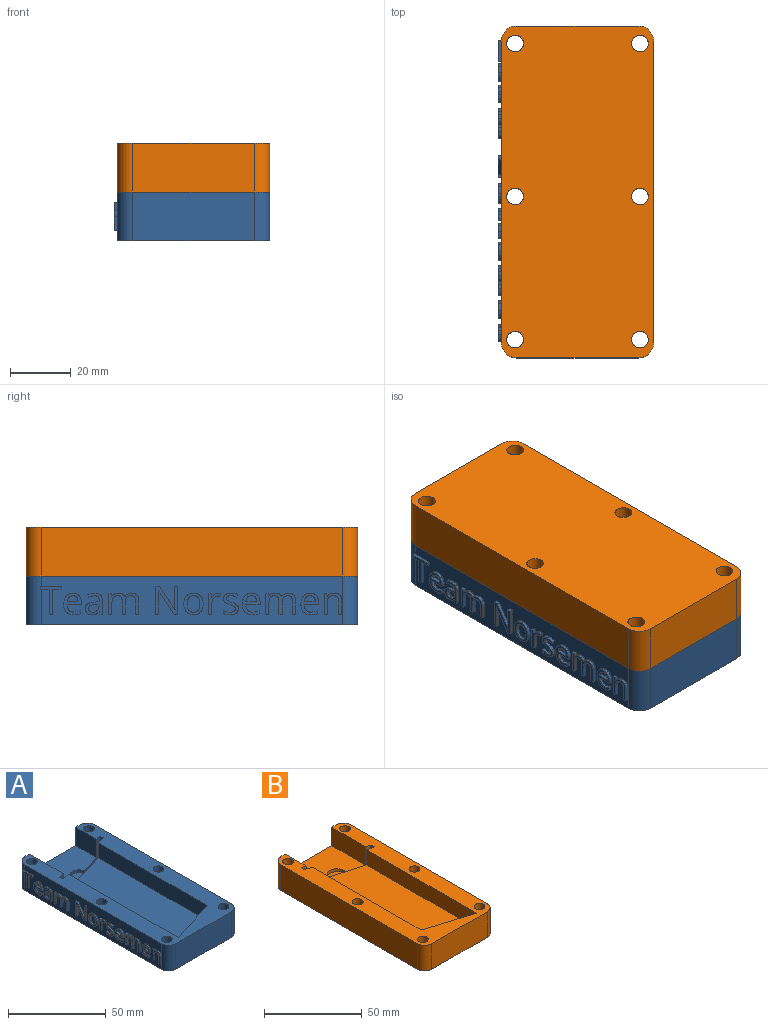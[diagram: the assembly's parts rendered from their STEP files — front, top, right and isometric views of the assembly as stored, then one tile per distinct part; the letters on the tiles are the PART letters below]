
ASSEMBLY  parts=2 mates=1
PART A: 282 faces, bbox 51x109x16 mm
  f0: plane 99x16mm, normal (-1,0,0), area 1307.5mm2, adj f2,f3,f26,f27,f28,f29,f30,f32
  f1: plane 40x16mm, normal (0,1,0), area 254.7mm2, adj f2,f3,f17,f18,f19,f278,f279
  f2: plane 109x50mm, normal (0,0,1), area 2115.1mm2, adj f0,f1,f4,f5,f6,f7,f8,f10
  f3: plane 109x50mm, normal (0,0,-1), area 5286mm2, adj f0,f1,f4,f5,f10,f11,f12,f13
  f4: plane 99x16mm, normal (1,0,0), area 1584mm2, adj f2,f3,f279,f281
  f5: plane 40x16mm, normal (0,-1,0), area 640mm2, adj f2,f3,f280,f281
  f6: plane 79.43x9.5mm, normal (1,0,0), area 754.5mm2, adj f2,f7,f9,f16
  f7: plane 30.5x9.5mm, normal (-0.3,0.95,0), area 303.5mm2, adj f2,f6,f8,f9
  f8: plane 78.57x9.5mm, normal (-1,0,0), area 746.5mm2, adj f2,f7,f9,f16
  f9: plane 88.07x30.5mm, normal (0,0,1), area 2409.5mm2, adj f6,f7,f8,f16
  f10: cylinder r=2.75mm len=16mm, axis (0,0,1), area 276.5mm2, adj f2,f3
  f11: cylinder r=2.75mm len=16mm, axis (0,0,1), area 276.5mm2, adj f2,f3
  f12: cylinder r=2.75mm len=16mm, axis (0,0,1), area 276.5mm2, adj f2,f3
  f13: cylinder r=2.75mm len=16mm, axis (0,0,1), area 276.5mm2, adj f2,f3
  f14: cylinder r=2.75mm len=16mm, axis (0,0,1), area 276.5mm2, adj f2,f3
  f15: cylinder r=2.75mm len=16mm, axis (0,0,1), area 276.5mm2, adj f2,f3
  f16: plane 39.93x13.3mm, normal (-0.27,0.96,0), area 250.8mm2, adj f2,f6,f8,f9,f21,f24,f25
  f17: plane 24.51x11.5mm, normal (1,0,0), area 281.8mm2, adj f1,f2,f19,f20
  f18: plane 15.01x11.5mm, normal (-1,0,0), area 172.6mm2, adj f1,f2,f19,f22
  f19: plane 33.5x24.51mm, normal (0,0,1), area 622.5mm2, adj f1,f17,f18,f20,f22,f23
  f20: plane 15.15x13.3mm, normal (0.27,-0.96,0), area 74.6mm2, adj f2,f17,f19,f23,f24,f25
  f21: plane 13.3x2.31mm, normal (-0.96,-0.27,0), area 31.9mm2, adj f2,f16,f22,f25
  f22: plane 15.15x13.3mm, normal (0.27,-0.96,0), area 58.9mm2, adj f2,f18,f19,f21,f23,f25
  f23: cylinder r=5mm len=9.81mm, axis (0,0,1), area 28.3mm2, adj f19,f20,f22,f25
  f24: plane 13.3x2.31mm, normal (0.96,0.27,0), area 31.9mm2, adj f2,f16,f20,f25
  f25: plane 40.58x13.63mm, normal (0,0,1), area 138.9mm2, adj f16,f20,f21,f22,f23,f24
  f26: plane 1.07x1mm, normal (0,0,-1), area 1.1mm2, adj f0,f27,f33,f34
  f27: plane 8.26x1mm, normal (0,-1,0), area 8.3mm2, adj f0,f26,f28,f34
  f28: plane 2.92x1mm, normal (0,0,-1), area 2.9mm2, adj f0,f27,f29,f34
  f29: plane 1x0.95mm, normal (0,-1,0), area 1mm2, adj f0,f28,f30,f34
  f30: plane 6.9x1.02mm, normal (0,0,1), area 6.9mm2, adj f0,f29,f31,f34,f278
  f31: plane 1.02x0.95mm, normal (0,1,0), area 1mm2, adj f30,f32,f34,f278
  f32: plane 2.92x1.02mm, normal (0,0,-1), area 2.9mm2, adj f0,f31,f33,f34,f278
  f33: plane 8.26x1mm, normal (0,1,0), area 8.3mm2, adj f0,f26,f32,f34
  f34: plane 9.21x6.9mm, normal (-1,0,0), area 15.4mm2, adj f26,f27,f28,f29,f30,f31,f32,f33
  f35: extruded ~1.33x1mm, area 1.5mm2, adj f36,f53,f54,f55
  f36: extruded ~1.26x1mm, area 1.4mm2, adj f35,f37,f54,f55
  f37: extruded ~1.51x1mm, area 1.6mm2, adj f36,f38,f54,f55
  f38: plane 3.61x1mm, normal (0,0,1), area 3.6mm2, adj f37,f53,f54,f55
  f39: extruded ~2.42x1mm, area 2.7mm2, adj f0,f40,f52,f54
  f40: extruded ~1.19x1mm, area 1.2mm2, adj f0,f39,f41,f54
  f41: extruded ~1.05x1mm, area 1.1mm2, adj f0,f40,f42,f54
  f42: plane 1x0.93mm, normal (0,-1,0), area 0.9mm2, adj f0,f41,f43,f54
  f43: extruded ~2.2x1mm, area 2.3mm2, adj f0,f42,f44,f54
  f44: extruded ~1.64x1mm, area 1.8mm2, adj f0,f43,f45,f54
  f45: extruded ~1.84x1mm, area 2mm2, adj f0,f44,f46,f54
  f46: plane 4.75x1mm, normal (0,0,-1), area 4.8mm2, adj f0,f45,f47,f54
  f47: plane 1x0.66mm, normal (0,-1,0), area 0.7mm2, adj f0,f46,f48,f54
  f48: extruded ~2.25x1mm, area 2.4mm2, adj f0,f47,f49,f54
  f49: extruded ~2.05x1mm, area 2.3mm2, adj f0,f48,f50,f54
  f50: extruded ~2.21x1mm, area 2.5mm2, adj f0,f49,f51,f54
  f51: extruded ~2.65x1mm, area 2.8mm2, adj f0,f50,f52,f54
  f52: extruded ~2.59x1mm, area 2.8mm2, adj f0,f39,f51,f54
  f53: extruded ~1.5x1mm, area 1.6mm2, adj f35,f38,f54,f55
  f54: plane 7.16x5.84mm, normal (-1,0,0), area 19mm2, adj f35,f36,f37,f38,f39,f40,f41,f42
  f55: plane 3.61x2.04mm, normal (-1,0,0), area 5.9mm2, adj f35,f36,f37,f38,f53
  f56: extruded ~1.53x1mm, area 1.7mm2, adj f57,f82,f83,f84
  f57: extruded ~1x0.96mm, area 1mm2, adj f56,f58,f83,f84
  f58: extruded ~1x0.86mm, area 1mm2, adj f57,f59,f83,f84
  f59: extruded ~1.07x1mm, area 1.3mm2, adj f58,f60,f83,f84
  f60: extruded ~1.8x1mm, area 1.9mm2, adj f59,f61,f83,f84
  f61: plane 1.05x1mm, normal (0,-0.04,-1), area 1mm2, adj f60,f62,f83,f84
  f62: plane 1x0.62mm, normal (0,1,0), area 0.6mm2, adj f61,f82,f83,f84
  f63: plane 1x0.98mm, normal (0,0.98,-0.21), area 1mm2, adj f0,f64,f81,f83
  f64: plane 1x0.78mm, normal (0,0,-1), area 0.8mm2, adj f0,f63,f65,f83
  f65: plane 4.71x1mm, normal (0,-1,0), area 4.7mm2, adj f0,f64,f66,f83
  f66: extruded ~1.76x1mm, area 1.9mm2, adj f0,f65,f67,f83
  f67: extruded ~1.83x1mm, area 2mm2, adj f0,f66,f68,f83
  f68: extruded ~1.22x1mm, area 1.2mm2, adj f0,f67,f69,f83
  f69: extruded ~1.12x1mm, area 1.2mm2, adj f0,f68,f70,f83
  f70: plane 1x0.8mm, normal (0,0.93,-0.37), area 0.9mm2, adj f0,f69,f71,f83
  f71: extruded ~1.95x1mm, area 2mm2, adj f0,f70,f72,f83
  f72: extruded ~1.12x1mm, area 1.2mm2, adj f0,f71,f73,f83
  f73: extruded ~1.2x1mm, area 1.3mm2, adj f0,f72,f74,f83
  f74: plane 1x0.43mm, normal (0,1,0), area 0.4mm2, adj f0,f73,f75,f83
  f75: plane 1.17x1mm, normal (0,0.03,1), area 1.2mm2, adj f0,f74,f76,f83
  f76: extruded ~3.34x2.19mm, area 4.5mm2, adj f0,f75,f77,f83
  f77: extruded ~1.51x1mm, area 1.7mm2, adj f0,f76,f78,f83
  f78: extruded ~1.61x1mm, area 1.7mm2, adj f0,f77,f79,f83
  f79: extruded ~1.28x1mm, area 1.3mm2, adj f0,f78,f80,f83
  f80: extruded ~1.03x1mm, area 1.4mm2, adj f0,f79,f81,f83
  f81: plane 1x0.05mm, normal (0,0,-1), area 0.1mm2, adj f0,f63,f80,f83
  f82: extruded ~1.5x1mm, area 1.6mm2, adj f56,f62,f83,f84
  f83: plane 7.14x5.54mm, normal (-1,0,0), area 18.7mm2, adj f56,f57,f58,f59,f60,f61,f62,f63
  f84: plane 3.39x2.66mm, normal (-1,0,0), area 7.3mm2, adj f56,f57,f58,f59,f60,f61,f62,f82
  f85: plane 4.49x1mm, normal (0,1,0), area 4.5mm2, adj f0,f86,f112,f113
  f86: plane 1.04x1mm, normal (0,0,-1), area 1mm2, adj f0,f85,f87,f113
  f87: plane 4.5x1mm, normal (0,-1,0), area 4.5mm2, adj f0,f86,f88,f113
  f88: extruded ~1.93x1mm, area 2.1mm2, adj f0,f87,f89,f113
  f89: extruded ~1.75x1mm, area 1.9mm2, adj f0,f88,f90,f113
  f90: extruded ~1.34x1mm, area 1.4mm2, adj f0,f89,f91,f113
  f91: extruded ~1x0.89mm, area 1.3mm2, adj f0,f90,f92,f113
  f92: plane 1x0.05mm, normal (0,0,1), area 0.1mm2, adj f0,f91,f93,f113
  f93: extruded ~2.12x1.17mm, area 2.6mm2, adj f0,f92,f94,f113
  f94: extruded ~1.21x1mm, area 1.3mm2, adj f0,f93,f95,f113
  f95: extruded ~1x0.84mm, area 1.2mm2, adj f0,f94,f96,f113
  f96: plane 1x0.05mm, normal (0,0,1), area 0.1mm2, adj f0,f95,f97,f113
  f97: plane 1x0.95mm, normal (0,-0.98,0.18), area 1mm2, adj f0,f96,f98,f113
  f98: plane 1x0.85mm, normal (0,0,1), area 0.9mm2, adj f0,f97,f99,f113
  f99: plane 6.9x1mm, normal (0,1,0), area 6.9mm2, adj f0,f98,f100,f113
  f100: plane 1.05x1mm, normal (0,0,-1), area 1mm2, adj f0,f99,f101,f113
  f101: plane 3.62x1mm, normal (0,-1,0), area 3.6mm2, adj f0,f100,f102,f113
  f102: extruded ~1.93x1mm, area 2mm2, adj f0,f101,f103,f113
  f103: extruded ~1.44x1mm, area 1.6mm2, adj f0,f102,f104,f113
  f104: extruded ~1.1x1mm, area 1.2mm2, adj f0,f103,f105,f113
  f105: extruded ~1.24x1mm, area 1.3mm2, adj f0,f104,f106,f113
  f106: plane 4.49x1mm, normal (0,1,0), area 4.5mm2, adj f0,f105,f107,f113
  f107: plane 1.05x1mm, normal (0,0,-1), area 1mm2, adj f0,f106,f108,f113
  f108: plane 3.85x1mm, normal (0,-1,0), area 3.9mm2, adj f0,f107,f109,f113
  f109: extruded ~1.73x1mm, area 1.8mm2, adj f0,f108,f110,f113
  f110: extruded ~1.44x1mm, area 1.6mm2, adj f0,f109,f111,f113
  f111: extruded ~1.1x1mm, area 1.2mm2, adj f0,f110,f112,f113
  f112: extruded ~1.24x1mm, area 1.3mm2, adj f0,f85,f111,f113
  f113: plane 9.84x7.03mm, normal (-1,0,0), area 27mm2, adj f85,f86,f87,f88,f89,f90,f91,f92
  f114: plane 1.22x1mm, normal (0,0,-1), area 1.2mm2, adj f0,f115,f128,f129
  f115: plane 9.21x1mm, normal (0,-1,0), area 9.2mm2, adj f0,f114,f116,f129
  f116: plane 1x1mm, normal (0,0,1), area 1mm2, adj f0,f115,f117,f129
  f117: plane 5.28x1mm, normal (0,1,0), area 5.3mm2, adj f0,f116,f118,f129
  f118: extruded ~1.32x1mm, area 1.3mm2, adj f0,f117,f119,f129
  f119: extruded ~1.09x1mm, area 1.1mm2, adj f0,f118,f120,f129
  f120: plane 1x0.05mm, normal (0,0,1), area 0.1mm2, adj f0,f119,f121,f129
  f121: plane 7.7x5.02mm, normal (0,-0.84,0.55), area 9.2mm2, adj f0,f120,f122,f129
  f122: plane 1.21x1mm, normal (0,0,1), area 1.2mm2, adj f0,f121,f123,f129
  f123: plane 9.21x1mm, normal (0,1,0), area 9.2mm2, adj f0,f122,f124,f129
  f124: plane 1x0.99mm, normal (0,0,-1), area 1mm2, adj f0,f123,f125,f129
  f125: plane 5.23x1mm, normal (0,-1,0), area 5.2mm2, adj f0,f124,f126,f129
  f126: extruded ~2.49x1mm, area 2.5mm2, adj f0,f125,f127,f129
  f127: plane 1x0.05mm, normal (0,0,-1), area 0.1mm2, adj f0,f126,f128,f129
  f128: plane 7.73x5.03mm, normal (0,0.84,-0.55), area 9.2mm2, adj f0,f114,f127,f129
  f129: plane 9.21x7.19mm, normal (-1,0,0), area 28mm2, adj f114,f115,f116,f117,f118,f119,f120,f121
  f130: extruded ~2.02x1mm, area 2.1mm2, adj f131,f146,f147,f148
  f131: extruded ~2.01x1mm, area 2.1mm2, adj f130,f132,f147,f148
  f132: extruded ~1.55x1mm, area 1.8mm2, adj f131,f133,f147,f148
  f133: extruded ~1.57x1mm, area 1.8mm2, adj f132,f134,f147,f148
  f134: extruded ~2x1mm, area 2.1mm2, adj f133,f135,f147,f148
  f135: extruded ~2.02x1mm, area 2.1mm2, adj f134,f136,f147,f148
  f136: extruded ~1.56x1mm, area 1.8mm2, adj f135,f146,f147,f148
  f137: extruded ~2.64x1mm, area 2.8mm2, adj f0,f138,f145,f147
  f138: extruded ~2.61x1mm, area 2.8mm2, adj f0,f137,f139,f147
  f139: extruded ~2.3x1mm, area 2.6mm2, adj f0,f138,f140,f147
  f140: extruded ~2.34x1mm, area 2.6mm2, adj f0,f139,f141,f147
  f141: extruded ~2.63x1mm, area 2.8mm2, adj f0,f140,f142,f147
  f142: extruded ~1.9x1mm, area 2mm2, adj f0,f141,f143,f147
  f143: extruded ~1.25x1.11mm, area 1.7mm2, adj f0,f142,f144,f147
  f144: extruded ~1.64x1mm, area 1.7mm2, adj f0,f143,f145,f147
  f145: extruded ~2.35x1mm, area 2.6mm2, adj f0,f137,f144,f147
  f146: extruded ~1.55x1mm, area 1.8mm2, adj f130,f136,f147,f148
  f147: plane 7.16x6.34mm, normal (-1,0,0), area 18.3mm2, adj f130,f131,f132,f133,f134,f135,f136,f137
  f148: plane 5.39x4.18mm, normal (-1,0,0), area 18.7mm2, adj f130,f131,f132,f133,f134,f135,f136,f146
  f149: extruded ~1x0.82mm, area 0.8mm2, adj f0,f150,f161,f162
  f150: extruded ~1.19x1mm, area 1.3mm2, adj f0,f149,f151,f162
  f151: extruded ~1.04x1mm, area 1.4mm2, adj f0,f150,f152,f162
  f152: plane 1x0.05mm, normal (0,0,1), area 0.1mm2, adj f0,f151,f153,f162
  f153: plane 1.28x1mm, normal (0,-1,0.09), area 1.3mm2, adj f0,f152,f154,f162
  f154: plane 1x0.86mm, normal (0,0,1), area 0.9mm2, adj f0,f153,f155,f162
  f155: plane 6.9x1mm, normal (0,1,0), area 6.9mm2, adj f0,f154,f156,f162
  f156: plane 1.05x1mm, normal (0,0,-1), area 1mm2, adj f0,f155,f157,f162
  f157: plane 3.7x1mm, normal (0,-1,0), area 3.7mm2, adj f0,f156,f158,f162
  f158: extruded ~1.69x1mm, area 1.8mm2, adj f0,f157,f159,f162
  f159: extruded ~1.43x1mm, area 1.6mm2, adj f0,f158,f160,f162
  f160: extruded ~1x0.76mm, area 0.8mm2, adj f0,f159,f161,f162
  f161: plane 1x0.97mm, normal (0,-0.99,-0.15), area 1mm2, adj f0,f149,f160,f162
  f162: plane 7.03x3.97mm, normal (-1,0,0), area 9.9mm2, adj f149,f150,f151,f152,f153,f154,f155,f156
  f163: extruded ~1.49x1mm, area 1.7mm2, adj f0,f164,f187,f188
  f164: extruded ~1.14x1mm, area 1.3mm2, adj f0,f163,f165,f188
  f165: extruded ~1.66x1mm, area 1.9mm2, adj f0,f164,f166,f188
  f166: extruded ~1.21x1mm, area 1.3mm2, adj f0,f165,f167,f188
  f167: extruded ~1x0.46mm, area 0.6mm2, adj f0,f166,f168,f188
  f168: extruded ~1x0.47mm, area 0.5mm2, adj f0,f167,f169,f188
  f169: extruded ~1x0.64mm, area 0.8mm2, adj f0,f168,f170,f188
  f170: extruded ~1.12x1mm, area 1.2mm2, adj f0,f169,f171,f188
  f171: extruded ~1.88x1mm, area 1.9mm2, adj f0,f170,f172,f188
  f172: plane 1x0.85mm, normal (0,-0.92,-0.4), area 0.9mm2, adj f0,f171,f173,f188
  f173: extruded ~2.18x1mm, area 2.2mm2, adj f0,f172,f174,f188
  f174: extruded ~1.88x1mm, area 2mm2, adj f0,f173,f175,f188
  f175: extruded ~1.33x1mm, area 1.6mm2, adj f0,f174,f176,f188
  f176: extruded ~1x0.81mm, area 0.8mm2, adj f0,f175,f177,f188
  f177: extruded ~1x0.61mm, area 0.9mm2, adj f0,f176,f178,f188
  f178: extruded ~1.37x1mm, area 1.5mm2, adj f0,f177,f179,f188
  f179: extruded ~1.36x1mm, area 1.5mm2, adj f0,f178,f180,f188
  f180: extruded ~1x0.69mm, area 0.8mm2, adj f0,f179,f181,f188
  f181: extruded ~1x0.8mm, area 1mm2, adj f0,f180,f182,f188
  f182: extruded ~1.26x1mm, area 1.3mm2, adj f0,f181,f183,f188
  f183: extruded ~1.1x1mm, area 1.1mm2, adj f0,f182,f184,f188
  f184: extruded ~1.07x1mm, area 1.1mm2, adj f0,f183,f185,f188
  f185: plane 1x0.97mm, normal (0,1,0), area 1mm2, adj f0,f184,f186,f188
  f186: extruded ~2.14x1mm, area 2.2mm2, adj f0,f185,f187,f188
  f187: extruded ~2.02x1mm, area 2.1mm2, adj f0,f163,f186,f188
  f188: plane 7.16x4.89mm, normal (-1,0,0), area 14.6mm2, adj f163,f164,f165,f166,f167,f168,f169,f170
  f189: extruded ~1.33x1mm, area 1.5mm2, adj f190,f207,f208,f209
  f190: extruded ~1.26x1mm, area 1.4mm2, adj f189,f191,f208,f209
  f191: extruded ~1.51x1mm, area 1.6mm2, adj f190,f192,f208,f209
  f192: plane 3.61x1mm, normal (0,0,1), area 3.6mm2, adj f191,f207,f208,f209
  f193: extruded ~2.42x1mm, area 2.7mm2, adj f0,f194,f206,f208
  f194: extruded ~1.19x1mm, area 1.2mm2, adj f0,f193,f195,f208
  f195: extruded ~1.05x1mm, area 1.1mm2, adj f0,f194,f196,f208
  f196: plane 1x0.93mm, normal (0,-1,0), area 0.9mm2, adj f0,f195,f197,f208
  f197: extruded ~2.2x1mm, area 2.3mm2, adj f0,f196,f198,f208
  f198: extruded ~1.64x1mm, area 1.8mm2, adj f0,f197,f199,f208
  f199: extruded ~1.84x1mm, area 2mm2, adj f0,f198,f200,f208
  f200: plane 4.75x1mm, normal (0,0,-1), area 4.8mm2, adj f0,f199,f201,f208
  f201: plane 1x0.66mm, normal (0,-1,0), area 0.7mm2, adj f0,f200,f202,f208
  f202: extruded ~2.25x1mm, area 2.4mm2, adj f0,f201,f203,f208
  f203: extruded ~2.05x1mm, area 2.3mm2, adj f0,f202,f204,f208
  f204: extruded ~2.21x1mm, area 2.5mm2, adj f0,f203,f205,f208
  f205: extruded ~2.65x1mm, area 2.8mm2, adj f0,f204,f206,f208
  f206: extruded ~2.59x1mm, area 2.8mm2, adj f0,f193,f205,f208
  f207: extruded ~1.5x1mm, area 1.6mm2, adj f189,f192,f208,f209
  f208: plane 7.16x5.84mm, normal (-1,0,0), area 19mm2, adj f189,f190,f191,f192,f193,f194,f195,f196
  f209: plane 3.61x2.04mm, normal (-1,0,0), area 5.9mm2, adj f189,f190,f191,f192,f207
  f210: plane 4.49x1mm, normal (0,1,0), area 4.5mm2, adj f0,f211,f237,f238
  f211: plane 1.04x1mm, normal (0,0,-1), area 1mm2, adj f0,f210,f212,f238
  f212: plane 4.5x1mm, normal (0,-1,0), area 4.5mm2, adj f0,f211,f213,f238
  f213: extruded ~1.93x1mm, area 2.1mm2, adj f0,f212,f214,f238
  f214: extruded ~1.75x1mm, area 1.9mm2, adj f0,f213,f215,f238
  f215: extruded ~1.34x1mm, area 1.4mm2, adj f0,f214,f216,f238
  f216: extruded ~1x0.89mm, area 1.3mm2, adj f0,f215,f217,f238
  f217: plane 1x0.05mm, normal (0,0,1), area 0.1mm2, adj f0,f216,f218,f238
  f218: extruded ~2.12x1.17mm, area 2.6mm2, adj f0,f217,f219,f238
  f219: extruded ~1.21x1mm, area 1.3mm2, adj f0,f218,f220,f238
  f220: extruded ~1x0.84mm, area 1.2mm2, adj f0,f219,f221,f238
  f221: plane 1x0.05mm, normal (0,0,1), area 0.1mm2, adj f0,f220,f222,f238
  f222: plane 1x0.95mm, normal (0,-0.98,0.18), area 1mm2, adj f0,f221,f223,f238
  f223: plane 1x0.85mm, normal (0,0,1), area 0.9mm2, adj f0,f222,f224,f238
  f224: plane 6.9x1mm, normal (0,1,0), area 6.9mm2, adj f0,f223,f225,f238
  f225: plane 1.05x1mm, normal (0,0,-1), area 1mm2, adj f0,f224,f226,f238
  f226: plane 3.62x1mm, normal (0,-1,0), area 3.6mm2, adj f0,f225,f227,f238
  f227: extruded ~1.93x1mm, area 2mm2, adj f0,f226,f228,f238
  f228: extruded ~1.44x1mm, area 1.6mm2, adj f0,f227,f229,f238
  f229: extruded ~1.1x1mm, area 1.2mm2, adj f0,f228,f230,f238
  f230: extruded ~1.24x1mm, area 1.3mm2, adj f0,f229,f231,f238
  f231: plane 4.49x1mm, normal (0,1,0), area 4.5mm2, adj f0,f230,f232,f238
  f232: plane 1.05x1mm, normal (0,0,-1), area 1mm2, adj f0,f231,f233,f238
  f233: plane 3.85x1mm, normal (0,-1,0), area 3.9mm2, adj f0,f232,f234,f238
  f234: extruded ~1.73x1mm, area 1.8mm2, adj f0,f233,f235,f238
  f235: extruded ~1.44x1mm, area 1.6mm2, adj f0,f234,f236,f238
  f236: extruded ~1.1x1mm, area 1.2mm2, adj f0,f235,f237,f238
  f237: extruded ~1.24x1mm, area 1.3mm2, adj f0,f210,f236,f238
  f238: plane 9.84x7.03mm, normal (-1,0,0), area 27mm2, adj f210,f211,f212,f213,f214,f215,f216,f217
  f239: extruded ~1.33x1mm, area 1.5mm2, adj f240,f257,f258,f259
  f240: extruded ~1.26x1mm, area 1.4mm2, adj f239,f241,f258,f259
  f241: extruded ~1.51x1mm, area 1.6mm2, adj f240,f242,f258,f259
  f242: plane 3.61x1mm, normal (0,0,1), area 3.6mm2, adj f241,f257,f258,f259
  f243: extruded ~2.42x1mm, area 2.7mm2, adj f0,f244,f256,f258
  f244: extruded ~1.19x1mm, area 1.2mm2, adj f0,f243,f245,f258
  f245: extruded ~1.05x1mm, area 1.1mm2, adj f0,f244,f246,f258
  f246: plane 1x0.93mm, normal (0,-1,0), area 0.9mm2, adj f0,f245,f247,f258
  f247: extruded ~2.2x1mm, area 2.3mm2, adj f0,f246,f248,f258
  f248: extruded ~1.64x1mm, area 1.8mm2, adj f0,f247,f249,f258
  f249: extruded ~1.84x1mm, area 2mm2, adj f0,f248,f250,f258
  f250: plane 4.75x1mm, normal (0,0,-1), area 4.8mm2, adj f0,f249,f251,f258
  f251: plane 1x0.66mm, normal (0,-1,0), area 0.7mm2, adj f0,f250,f252,f258
  f252: extruded ~2.25x1mm, area 2.4mm2, adj f0,f251,f253,f258
  f253: extruded ~2.05x1mm, area 2.3mm2, adj f0,f252,f254,f258
  f254: extruded ~2.21x1mm, area 2.5mm2, adj f0,f253,f255,f258
  f255: extruded ~2.65x1mm, area 2.8mm2, adj f0,f254,f256,f258
  f256: extruded ~2.59x1mm, area 2.8mm2, adj f0,f243,f255,f258
  f257: extruded ~1.5x1mm, area 1.6mm2, adj f239,f242,f258,f259
  f258: plane 7.16x5.84mm, normal (-1,0,0), area 19mm2, adj f239,f240,f241,f242,f243,f244,f245,f246
  f259: plane 3.61x2.04mm, normal (-1,0,0), area 5.9mm2, adj f239,f240,f241,f242,f257
  f260: plane 4.47x1mm, normal (0,1,0), area 4.5mm2, adj f0,f261,f276,f277
  f261: plane 1.05x1mm, normal (0,0,-1), area 1mm2, adj f0,f260,f262,f277
  f262: plane 4.5x1mm, normal (0,-1,0), area 4.5mm2, adj f0,f261,f263,f277
  f263: extruded ~1.93x1mm, area 2.1mm2, adj f0,f262,f264,f277
  f264: extruded ~1.88x1mm, area 2mm2, adj f0,f263,f265,f277
  f265: extruded ~1.29x1mm, area 1.3mm2, adj f0,f264,f266,f277
  f266: extruded ~1x0.9mm, area 1.2mm2, adj f0,f265,f267,f277
  f267: plane 1x0.05mm, normal (0,0,1), area 0.1mm2, adj f0,f266,f268,f277
  f268: plane 1x0.95mm, normal (0,-0.98,0.18), area 1mm2, adj f0,f267,f269,f277
  f269: plane 1x0.85mm, normal (0,0,1), area 0.9mm2, adj f0,f268,f270,f277
  f270: plane 6.9x1mm, normal (0,1,0), area 6.9mm2, adj f0,f269,f271,f277
  f271: plane 1.05x1mm, normal (0,0,-1), area 1mm2, adj f0,f270,f272,f277
  f272: plane 3.62x1mm, normal (0,-1,0), area 3.6mm2, adj f0,f271,f273,f277
  f273: extruded ~1.93x1mm, area 2mm2, adj f0,f272,f274,f277
  f274: extruded ~1.59x1mm, area 1.7mm2, adj f0,f273,f275,f277
  f275: extruded ~1.2x1mm, area 1.3mm2, adj f0,f274,f276,f277
  f276: extruded ~1.26x1mm, area 1.3mm2, adj f0,f260,f275,f277
  f277: plane 7.03x5.77mm, normal (-1,0,0), area 17.3mm2, adj f260,f261,f262,f263,f264,f265,f266,f267
  f278: cylinder r=5mm len=16mm, axis (0,0,1), area 125.3mm2, adj f0,f1,f2,f3,f30,f31,f32
  f279: cylinder r=5mm len=16mm, axis (0,0,-1), area 125.7mm2, adj f1,f2,f3,f4
  f280: cylinder r=5mm len=16mm, axis (0,0,-1), area 125.7mm2, adj f0,f2,f3,f5
  f281: cylinder r=5mm len=16mm, axis (0,0,1), area 125.7mm2, adj f2,f3,f4,f5
PART B: 30 faces, bbox 50x109x16 mm
  f0: plane 109x50mm, normal (0,0,1), area 2116.3mm2, adj f1,f2,f3,f6,f7,f8,f9,f10
  f1: plane 40x16mm, normal (0,1,0), area 254.7mm2, adj f0,f5,f17,f18,f19,f20,f21
  f2: plane 78.57x9.5mm, normal (1,0,0), area 746.5mm2, adj f0,f4,f9,f16
  f3: plane 79.43x9.5mm, normal (-1,0,0), area 754.5mm2, adj f0,f4,f9,f16
  f4: plane 88.07x30.5mm, normal (0,0,1), area 2409.5mm2, adj f2,f3,f9,f16
  f5: plane 109x50mm, normal (0,0,-1), area 5286mm2, adj f1,f6,f7,f8,f10,f11,f12,f13
  f6: plane 99x16mm, normal (1,0,0), area 1584mm2, adj f0,f5,f21,f23
  f7: plane 99x16mm, normal (-1,0,0), area 1584mm2, adj f0,f5,f20,f22
  f8: plane 40x16mm, normal (0,-1,0), area 640mm2, adj f0,f5,f22,f23
  f9: plane 30.5x9.5mm, normal (0.3,0.95,0), area 303.5mm2, adj f0,f2,f3,f4
  f10: cylinder r=2.75mm len=16mm, axis (0,0,1), area 276.5mm2, adj f0,f5
  f11: cylinder r=2.75mm len=16mm, axis (0,0,1), area 276.5mm2, adj f0,f5
  f12: cylinder r=2.75mm len=16mm, axis (0,0,1), area 276.5mm2, adj f0,f5
  f13: cylinder r=2.75mm len=16mm, axis (0,0,1), area 276.5mm2, adj f0,f5
  f14: cylinder r=2.75mm len=16mm, axis (0,0,1), area 276.5mm2, adj f0,f5
  f15: cylinder r=2.75mm len=16mm, axis (0,0,1), area 276.5mm2, adj f0,f5
  f16: plane 39.93x13.3mm, normal (0.27,0.96,0), area 250.8mm2, adj f0,f2,f3,f4,f25,f28,f29
  f17: plane 15.01x11.5mm, normal (1,0,0), area 172.6mm2, adj f0,f1,f19,f24
  f18: plane 24.51x11.5mm, normal (-1,0,0), area 281.8mm2, adj f0,f1,f19,f26
  f19: plane 33.5x24.51mm, normal (0,0,1), area 622.5mm2, adj f1,f17,f18,f24,f26,f27
  f20: cylinder r=5mm len=16mm, axis (0,0,1), area 125.7mm2, adj f0,f1,f5,f7
  f21: cylinder r=5mm len=16mm, axis (0,0,-1), area 125.7mm2, adj f0,f1,f5,f6
  f22: cylinder r=5mm len=16mm, axis (0,0,-1), area 125.7mm2, adj f0,f5,f7,f8
  f23: cylinder r=5mm len=16mm, axis (0,0,1), area 125.7mm2, adj f0,f5,f6,f8
  f24: plane 15.15x13.3mm, normal (-0.27,-0.96,0), area 58.9mm2, adj f0,f17,f19,f27,f28,f29
  f25: plane 13.3x2.58mm, normal (-0.99,-0.11,0), area 34.5mm2, adj f0,f16,f26,f29
  f26: plane 14.2x13.3mm, normal (-0.27,-0.96,0), area 61.4mm2, adj f0,f18,f19,f25,f27,f29
  f27: cylinder r=5mm len=9.81mm, axis (0,0,1), area 28.3mm2, adj f19,f24,f26,f29
  f28: plane 13.3x2.31mm, normal (0.96,-0.27,0), area 31.9mm2, adj f0,f16,f24,f29
  f29: plane 39.93x13.63mm, normal (0,0,1), area 137.7mm2, adj f16,f24,f25,f26,f27,f28
PLACE A t=(15.98,0.31,-5.3)mm
PLACE B rot(axis=(0,1,0),180deg) t=(15.98,0.31,26.7)mm
MATE fastened B.f14 <-> A.f12  axis (0,0,-1) through (36.48,-1.19,10.7)mm
